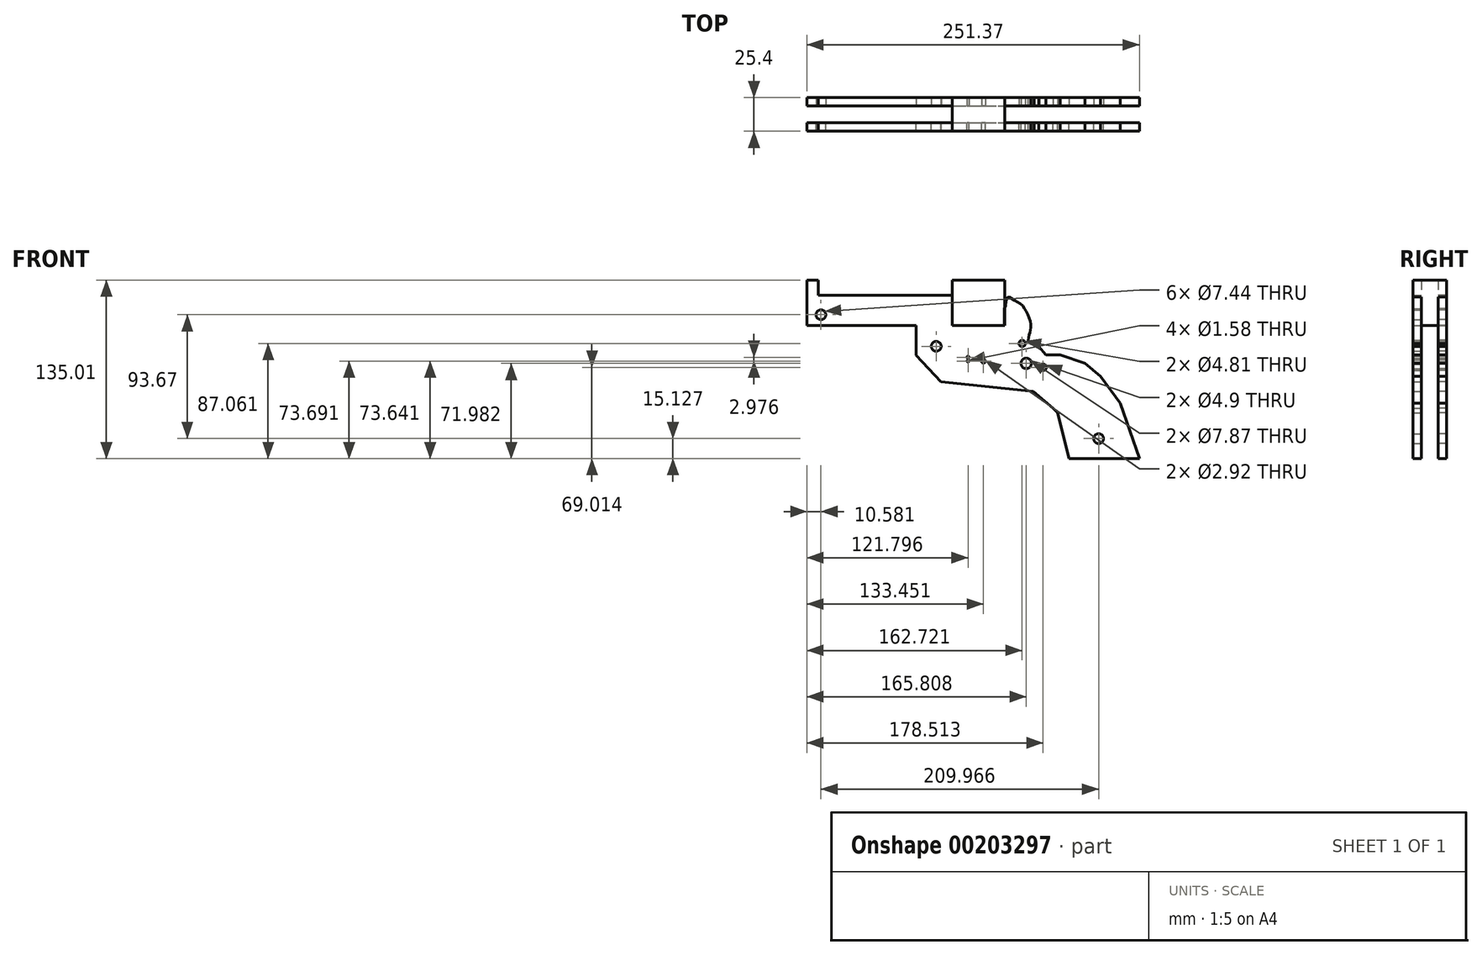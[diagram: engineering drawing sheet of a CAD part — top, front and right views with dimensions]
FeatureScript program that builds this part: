
annotation { "Feature Type Name" : "Feature", "Feature Type Description" : "" }
export const myFeature = defineFeature(function(context is Context, id is Id, definition is map)
    precondition{}
    {
        {
            var Q0;
            Q0=qCreatedBy(makeId("Front.planeOp"),FACE);
            var sketch = newSketch(context, id + "F0", { "sketchPlane" : qUnion([Q0])});
            skCircle(sketch, "E0", {"center": v(-18.07, -4.33) * mm, "radius": 1.46 * mm});
            skCircle(sketch, "E1", {"center": v(11.2, 9.1) * mm, "radius": 2.4 * mm});
            skCircle(sketch, "E2", {"center": v(27, -8.96) * mm, "radius": 2.45 * mm});
            skCircle(sketch, "E3", {"center": v(14.29, -5.99) * mm, "radius": 3.93 * mm});
            skCircle(sketch, "E4", {"center": v(-53.75, 6.93) * mm, "radius": 3.72 * mm});
            skCircle(sketch, "E5", {"center": v(-29.72, -4.28) * mm, "radius": 0.79 * mm});
            skLineSegment(sketch, "E6", {"start": v(-2.22, 35.23) * mm, "end": v(-2.22, 22.69) * mm});
            skLineSegment(sketch, "E7", {"start": v(-68.84, 22.69) * mm, "end": v(-68.84, 0) * mm});
            skLineSegment(sketch, "E8", {"start": v(-50.18, -19.78) * mm, "end": v(19.66, -27.1) * mm});
            skLineSegment(sketch, "E9", {"start": v(19.66, -27.1) * mm, "end": v(34.59, -39.9) * mm});
            skLineSegment(sketch, "E10", {"start": v(34.59, -39.9) * mm, "end": v(38.18, -43.36) * mm});
            skLineSegment(sketch, "E11", {"start": v(38.18, -43.36) * mm, "end": v(46.5, -77.97) * mm});
            skLineSegment(sketch, "E12", {"start": v(99.85, -77.97) * mm, "end": v(85.36, -35.94) * mm});
            skLineSegment(sketch, "E13", {"start": v(85.36, -35.94) * mm, "end": v(70.42, -15.8) * mm});
            skLineSegment(sketch, "E14", {"start": v(70.42, -15.8) * mm, "end": v(58.83, -5.89) * mm});
            skLineSegment(sketch, "E15", {"start": v(58.83, -5.89) * mm, "end": v(39.86, 0.5) * mm});
            skLineSegment(sketch, "E16", {"start": v(39.86, 0.5) * mm, "end": v(29.1, 0.5) * mm});
            skLineSegment(sketch, "E17", {"start": v(29.1, 0.5) * mm, "end": v(23.9, 6.67) * mm});
            skLineSegment(sketch, "E18", {"start": v(23.9, 6.67) * mm, "end": v(20.1, 8.97) * mm});
            skLineSegment(sketch, "E19", {"start": v(20.1, 8.97) * mm, "end": v(17.51, 8.97) * mm});
            skFitSpline(sketch, "E20", {"points": [v(17.51, 8.97) * mm, v(15.96, 11.2) * mm, v(16.5, 15.64) * mm, v(17.51, 19.5) * mm, v(17.51, 25.32) * mm, v(14.48, 32.88) * mm, v(10.46, 38.6) * mm, v(3.7, 42.72) * mm, v(0, 43.99) * mm, v(-2.22, 35.23) * mm], "startDerivative": vector(-27.68, 12.25) * mm, "endDerivative": vector(-28.6, -30.71) * mm});
            skLineSegment(sketch, "E21", {"start": v(-50.18, -19.78) * mm, "end": v(-68.84, 0) * mm});
            skLineSegment(sketch, "E22", {"start": v(46.5, -77.97) * mm, "end": v(99.85, -77.97) * mm});
            skLineSegment(sketch, "E23", {"start": v(-68.84, 22.69) * mm, "end": v(-2.22, 22.69) * mm});
            skLineSegment(sketch, "E24.bottom", {"start": v(-41.68, 22.69) * mm, "end": v(-151.52, 22.69) * mm});
            skLineSegment(sketch, "E24.left", {"start": v(-41.68, 22.69) * mm, "end": v(-41.68, 45.67) * mm});
            skLineSegment(sketch, "E24.right", {"start": v(-151.52, 22.69) * mm, "end": v(-151.52, 57.03) * mm});
            skLineSegment(sketch, "E25.top", {"start": v(-41.68, 22.69) * mm, "end": v(-2.22, 22.69) * mm});
            skCircle(sketch, "E26", {"center": v(-29.72, -1.3) * mm, "radius": 0.79 * mm});
            skLineSegment(sketch, "E27", {"start": v(-29.72, -4.28) * mm, "end": v(-29.72, -1.3) * mm});
            skLineSegment(sketch, "E28", {"start": v(-151.52, 57.03) * mm, "end": v(-142.83, 57.03) * mm});
            skLineSegment(sketch, "E29", {"start": v(-142.83, 57.03) * mm, "end": v(-142.83, 45.67) * mm});
            skLineSegment(sketch, "E30", {"start": v(-142.83, 45.67) * mm, "end": v(-41.68, 45.67) * mm});
            skCircle(sketch, "E31", {"center": v(-140.94, 30.83) * mm, "radius": 3.72 * mm});
            skCircle(sketch, "E32", {"center": v(69.03, -62.84) * mm, "radius": 3.72 * mm});
            skSolve(sketch);
        }
        {
            var Q0;
            Q0=qCreatedBy(makeId("Front.planeOp"),FACE);
            var sketch = newSketch(context, id + "F1", { "sketchPlane" : qUnion([Q0])});
            skLineSegment(sketch, "E33", {"start": v(-2.09, 35.1) * mm, "end": v(-2.09, 22.55) * mm});
            skLineSegment(sketch, "E34.left", {"start": v(-41.54, 22.55) * mm, "end": v(-41.54, 57.04) * mm});
            skLineSegment(sketch, "E35.top", {"start": v(-41.54, 22.55) * mm, "end": v(-2.09, 22.55) * mm});
            skLineSegment(sketch, "E35.left", {"start": v(-41.54, 57.04) * mm, "end": v(-41.54, 22.55) * mm});
            skLineSegment(sketch, "E36.bottom", {"start": v(-41.54, 57.04) * mm, "end": v(-2.09, 57.04) * mm});
            skLineSegment(sketch, "E36.right", {"start": v(-2.09, 57.04) * mm, "end": v(-2.09, 22.55) * mm});
            skSolve(sketch);
        }
        {
            var Q0;
            Q0 = qSketchRegion(id + "F1", true);
            extrude(context, id + "F2", {"entities" : qUnion([Q0]), "endBound" : BoundingType.SYMMETRIC, "depth" : 25.4 * mm});
        }
        {
            var Q0;
            Q0 = qSketchRegion(id + "F0", true);
            extrude(context, id + "F3", {"entities" : qUnion([Q0]), "depth" : 12.7 * mm, "hasSecondDirection" : true, "secondDirectionOppositeDirection" : false, "secondDirectionDepth" : 6.35 * mm});
        }
        {
            var Q0;
            Q0 = qSketchRegion(id + "F0", true);
            extrude(context, id + "F4", {"entities" : qUnion([Q0]), "oppositeDirection" : true, "depth" : 12.7 * mm, "hasSecondDirection" : true, "secondDirectionOppositeDirection" : true, "secondDirectionDepth" : 6.35 * mm});
        }
    });
